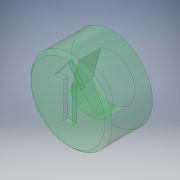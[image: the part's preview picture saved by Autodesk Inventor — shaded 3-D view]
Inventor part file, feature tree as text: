
AUTODESK INVENTOR PART (.ipt)
format: ipt  version: 2017 SP1 (Build 210196100, 196)  size: 159,744 bytes
history: native  units: in
note: dims shown in document units (in); Inventor stores cm internally (conversion verified against a paired STEP export)
features: extrude x5, sketch x5, projected_geometry x3, chamfer x1
ambient origin geometry x8: Origin, YZ Plane, XZ Plane, XY Plane, X Axis, Y Axis, Z Axis, Center Point
bodies: Solid1 (feature_tree)
feature tree (14):
  extrude  "Extrusion1"  Depth=0.0125in
  extrude  "Extrusion2"  Depth=0.1in
  extrude  "Extrusion3"  Depth=0.2in
  extrude  "Extrusion4"  Depth=0.05in
  extrude  "Extrusion5"  Depth=0.025in TaperAngle=0.0deg
  chamfer  "Chamfer1"  Angle=60.0deg  [1 undecoded]
  sketch  "Sketch1"  dims[d0=0.235in d2=0.0125in]
  sketch  "Sketch2"  dims[d3=1.0in d4=0.0in d5=0.1in]
  sketch  "Sketch3"  dims[d6=0.125in d7=0.0in d8=0.2in]
  sketch  "Sketch4"  dims[d9=0.1in d10=0.05in]
  projected_geometry  "Projected Loop1"
  projected_geometry  "Projected Loop2"
  sketch  "Sketch5"  dims[d11=0.15in d12=0.025in d13=0.0in d14=60.0deg d15=0.221in d16=0.4in d17=0.0in d18=0.25in d19=0.0in d20=0.02in d21=0.125in d22=45.0deg]
  projected_geometry  "Projected Loop3"
note: 1 required parameter value undecoded (feature->parameter linkage not recoverable at this tier; creation-order binding heuristic only, values carry confidence <= 0.55)
